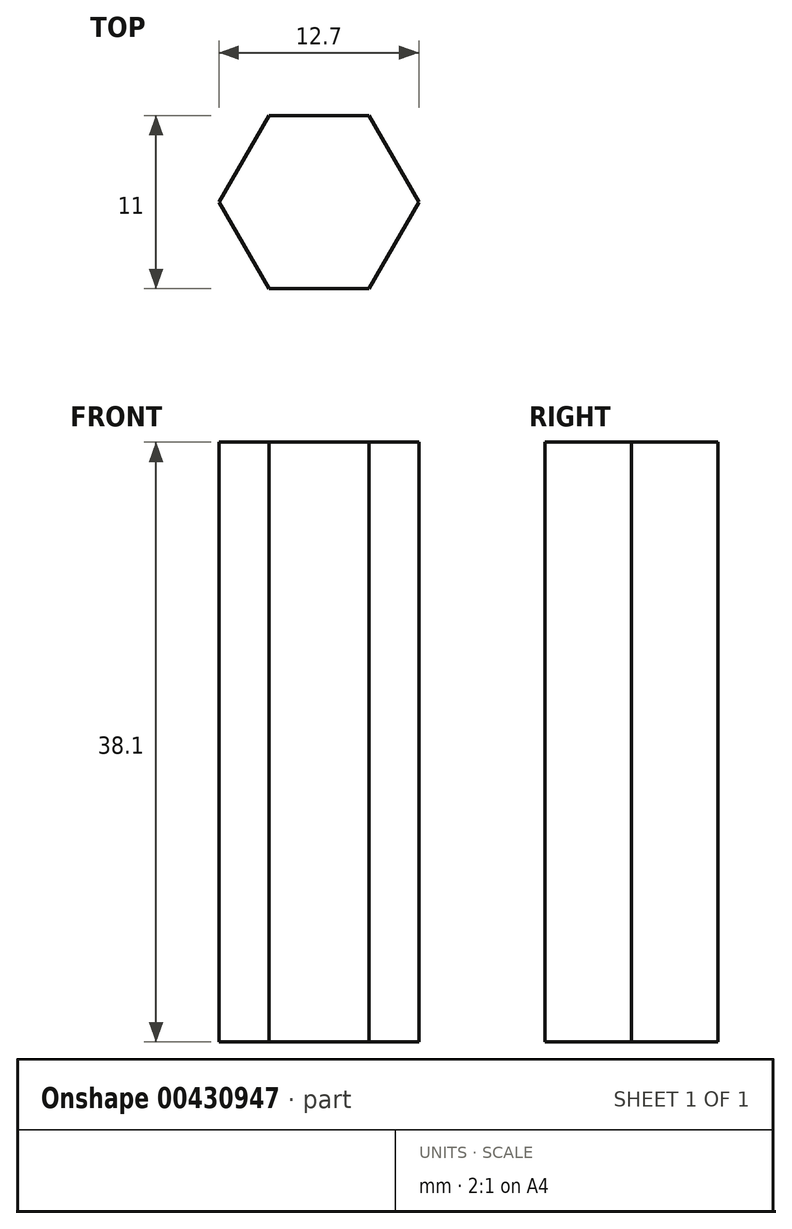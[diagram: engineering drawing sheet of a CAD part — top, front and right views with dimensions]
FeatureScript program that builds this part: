
annotation { "Feature Type Name" : "Feature", "Feature Type Description" : "" }
export const myFeature = defineFeature(function(context is Context, id is Id, definition is map)
    precondition{}
    {
        {
            var Q0;
            Q0=qCreatedBy(makeId("Top.planeOp"),FACE);
            var sketch = newSketch(context, id + "F0", { "sketchPlane" : qUnion([Q0])});
            skCircle(sketch, "E0.cCircle", {"center": v(0, 0) * mm, "radius": 6.35 * mm, "construction": true});
            skLineSegment(sketch, "E0.0", {"start": v(6.35, 0) * mm, "end": v(3.17, -5.5) * mm});
            skLineSegment(sketch, "E0.1", {"start": v(3.17, -5.5) * mm, "end": v(-3.18, -5.5) * mm});
            skLineSegment(sketch, "E0.2", {"start": v(-3.18, -5.5) * mm, "end": v(-6.35, 0) * mm});
            skLineSegment(sketch, "E0.3", {"start": v(-6.35, 0) * mm, "end": v(-3.17, 5.5) * mm});
            skLineSegment(sketch, "E0.4", {"start": v(-3.17, 5.5) * mm, "end": v(3.18, 5.5) * mm});
            skLineSegment(sketch, "E0.5", {"start": v(3.18, 5.5) * mm, "end": v(6.35, 0) * mm});
            skSolve(sketch);
        }
        {
            var Q0;
            Q0=makeQuery(id+"F0.imprint","IMPRINT",FACE,{"disambiguationData":[TD([[makeQuery(id+"F0.imprint","IMPRINT",EDGE,{"derivedFrom":sQuery(id+"F0.wireOp",EDGE,"E0.0")}),-1.0]])]});
            extrude(context, id + "F1", {"entities" : qUnion([Q0]), "depth" : 38.1 * mm});
        }
    });
